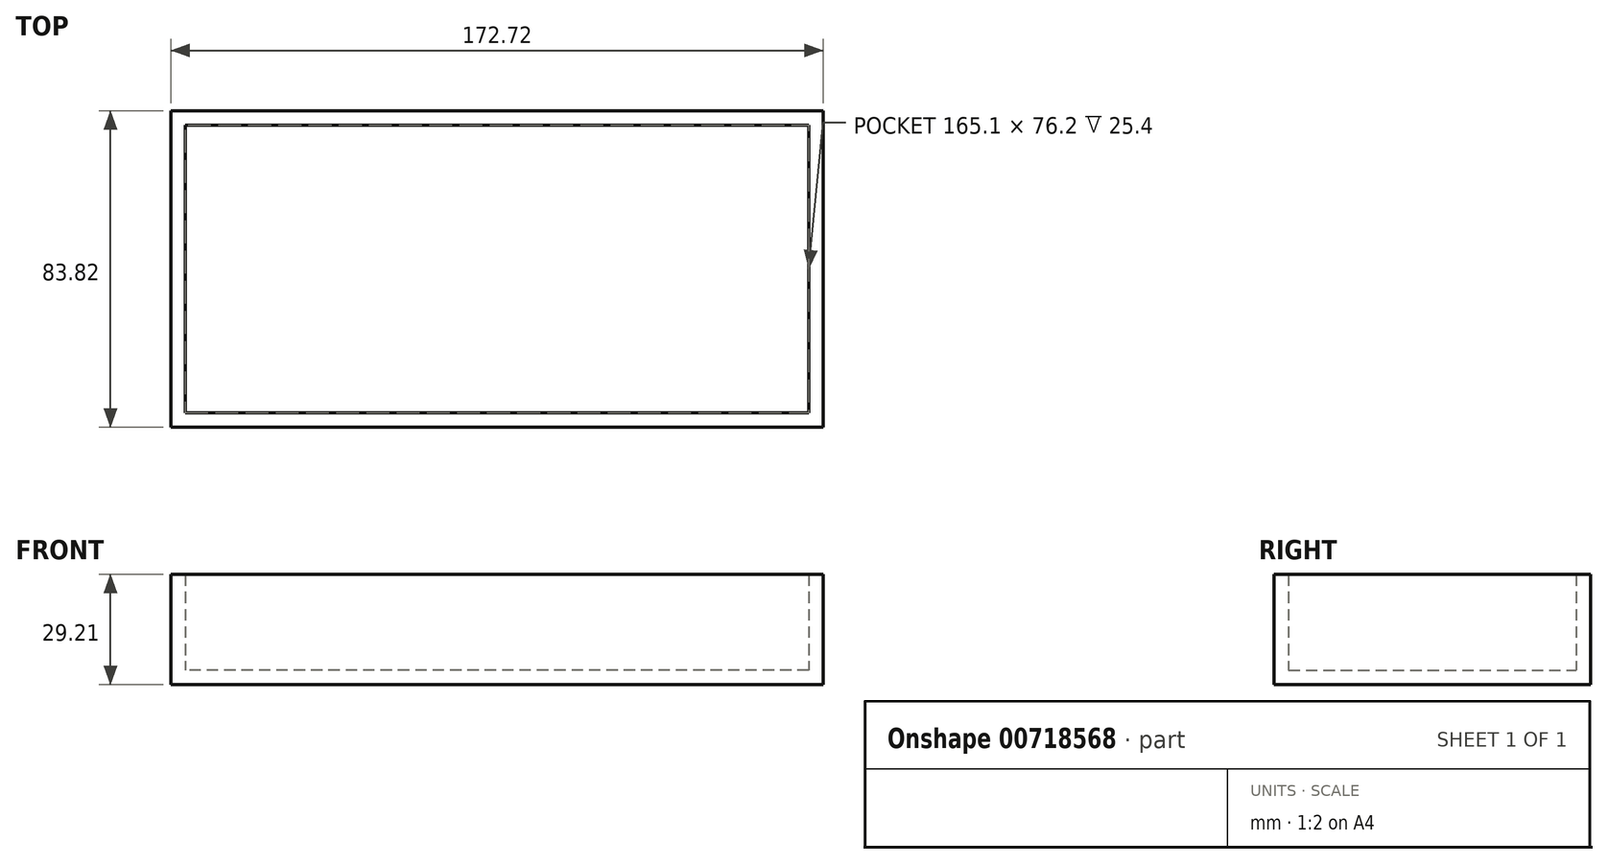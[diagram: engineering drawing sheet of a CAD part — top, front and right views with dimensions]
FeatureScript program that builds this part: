
annotation { "Feature Type Name" : "Feature", "Feature Type Description" : "" }
export const myFeature = defineFeature(function(context is Context, id is Id, definition is map)
    precondition{}
    {
        {
            var Q0;
            Q0=qCreatedBy(makeId("Top.planeOp"),FACE);
            var sketch = newSketch(context, id + "F0", { "sketchPlane" : qUnion([Q0])});
            skLineSegment(sketch, "E0.top", {"start": v(0, -3.81) * mm, "end": v(3.81, -3.81) * mm});
            skLineSegment(sketch, "E0.right", {"start": v(3.81, 0) * mm, "end": v(3.81, -3.81) * mm});
            skLineSegment(sketch, "E1.top", {"start": v(-165.1, 80) * mm, "end": v(-168.91, 80) * mm});
            skLineSegment(sketch, "E1.right", {"start": v(-168.91, 76.2) * mm, "end": v(-168.91, 80) * mm});
            skLineSegment(sketch, "E2.bottom", {"start": v(-168.91, 80) * mm, "end": v(3.8, 80) * mm});
            skLineSegment(sketch, "E2.top", {"start": v(-168.91, -3.81) * mm, "end": v(3.8, -3.81) * mm});
            skLineSegment(sketch, "E2.left", {"start": v(-168.91, 80) * mm, "end": v(-168.91, -3.81) * mm});
            skLineSegment(sketch, "E2.right", {"start": v(3.81, 80) * mm, "end": v(3.81, -3.81) * mm});
            skPoint(sketch, "E3.start.orphan", {"position": v(-165.1, 0) * mm});
            skPoint(sketch, "E4.start.orphan", {"position": v(0, 0) * mm});
            skSolve(sketch);
        }
        {
            var Q0;
            Q0 = qSketchRegion(id + "F0", true);
            extrude(context, id + "F1", {"entities" : qUnion([Q0]), "depth" : 3.8 * mm, "offsetDistance" : 25.4 * mm});
        }
        {
            var Q0;
            Q0=makeQuery(id+"F1.opExtrude","CAP_FACE",FACE,{"disambiguationData":[OSD([sQuery(id+"F0.wireOp",EDGE,"E2.bottom"),sQuery(id+"F0.wireOp",EDGE,"E2.top"),sQuery(id+"F0.wireOp",EDGE,"E2.left"),sQuery(id+"F0.wireOp",EDGE,"E2.right")])],"isStart":false});
            var sketch = newSketch(context, id + "F2", { "sketchPlane" : qUnion([Q0])});
            skLineSegment(sketch, "E5.bottom", {"start": v(0, 0) * mm, "end": v(-165.1, 0) * mm});
            skLineSegment(sketch, "E5.top", {"start": v(0, 76.2) * mm, "end": v(-165.1, 76.2) * mm});
            skLineSegment(sketch, "E5.left", {"start": v(0, 0) * mm, "end": v(0, 76.2) * mm});
            skLineSegment(sketch, "E5.right", {"start": v(-165.1, 0) * mm, "end": v(-165.1, 76.2) * mm});
            skLineSegment(sketch, "E6", {"start": v(0, -3.81) * mm, "end": v(3.81, -3.81) * mm});
            skLineSegment(sketch, "E7", {"start": v(3.81, -3.81) * mm, "end": v(3.81, 0) * mm});
            skLineSegment(sketch, "E8", {"start": v(-165.1, 80) * mm, "end": v(-168.91, 80) * mm});
            skLineSegment(sketch, "E9", {"start": v(-168.91, 80) * mm, "end": v(-168.91, 76.2) * mm});
            skLineSegment(sketch, "E10.bottom", {"start": v(3.8, -3.81) * mm, "end": v(-168.91, -3.81) * mm});
            skLineSegment(sketch, "E10.top", {"start": v(3.8, 80) * mm, "end": v(-168.91, 80) * mm});
            skLineSegment(sketch, "E10.left", {"start": v(3.81, -3.81) * mm, "end": v(3.81, 80) * mm});
            skLineSegment(sketch, "E10.right", {"start": v(-168.91, -3.81) * mm, "end": v(-168.91, 80) * mm});
            skSolve(sketch);
        }
        {
            var Q0;
            Q0 = qSketchRegion(id + "F2", true);
            extrude(context, id + "F3", {"entities" : qUnion([Q0]), "operationType" : NewBodyOperationType.ADD, "depth" : 25.4 * mm, "offsetDistance" : 25.4 * mm});
        }
    });
